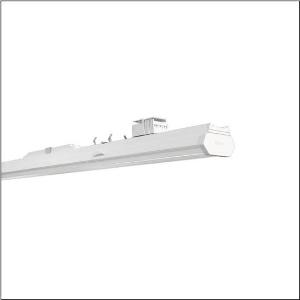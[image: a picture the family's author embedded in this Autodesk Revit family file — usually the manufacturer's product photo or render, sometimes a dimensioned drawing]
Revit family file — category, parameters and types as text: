
# Revit family: licross_11_protected_tw_51tp12tnt85x
name_source: partatom
category: Lighting Fixtures
units: mm (PartAtom-declared; Revit-internal decimal feet)

## family parameters
Cut with Voids When Loaded = No
Host = Face
Light Source = No
Part Type = Normal
Room Calculation Point = No
Round Connector Dimension = Use Diameter
Shared = No

## types (1)
- --- (1 x LED 2700 K ... 6500 K, 8840 lm, 56 W, 2700K)
    Apparent Load = 56 VA
    CIE Flux Codes = 70 91 97 98 100
    Color Rendering = 80
    Color Temperature = 2700K
    Default Elevation = 1800 mm
    Description = Licross 11 Protected TW, luminaire insert, of sheet steel, galvanised, coil coated, white, length: 1.500mm, width: 90mm, height: 101mm, LED rated luminous flux: 8.840lm, light colour: 8tw, SDCM (Standard Deviation of Colour Matching)MacAdam ≤ 2 SDCM (initial), control gear: DALI DT8, with plug, 5-pole, with phase selection, mains connection: 220..240V, AC, 50/60Hz, rated input power: 56W, internal wiring halogen-free, primary optical cover: cover, of PMMA, light emission: direct distribution, primary light characteristic: symmetric, protection rating (complete): IP64, insulation class (complete): insulation class I (protective earthing), certification: CE, ENEC, VDE, UKCA, protection symbol: D if used in an environment with conductive dust loads with corresponding accessories, impact resistance: IK06, permissible ambient temperature for indoor applications: -25..+35°C, corresponds to IFS (International Featured Standards) requirements for safety and quality in the food industry, reducing of maximum allowable ambient temperature of 5°C with ceiling mounting, LABS conformity tested according to VDMA 24364:2018-05, The light source and the operating device comply with the requirements of the Ecodesign Regulation (EU) 2019/2020 and are replaceable in accordance with this regulation, packaging unit: 1 piece
    Height = 92 mm
    Lamp = 1 x LED 2700 K ... 6500 K
    Lamp Light Flux = 8840 lm
    Lamp Power = 56 W
    Lamp count = 1
    Length = 1500 mm
    Luminous efficacy = 158 lm/W
    Manufacturer = Siteco
    ModVariant = No
    Model = 51TP12TNT85X
    Mounting Place = Ceiling
    Mounting Type = Pendant
    Number of Poles = 1
    OnlyDefault = Yes
    Power Factor = 1
    Product Name = Licross 11 Protected TW
    Product group = luminaire insert | ceiling pendant
    ProductGroupID = 901
    Protection Class = Protection class I
    Protection Degree = IP 64
    RLX_Detail_Level = 1
    RLX_Emergency_Light_Flux = 0 lm
    RLX_Emergency_Type = 0
    RLX_Emergency_Type_DB = No
    RlxData = <blob elided: 20993 chars, md5=54ca5dc1>
    Socket = socket
    Standby Power = 0 W
    System Light Flux = 8840 lm
    System Power = 56 W
    Type Comments = individual setting: CCT=2700K
    Type Image = l_1256148.jpg
    URL = http://relux.com
    VarID = @adj_057721
    Voltage = 0 V
    Weight = 0.00 kg
    Width = 88 mm

## geometry (parser evidence)
native form markers: Blend x4, Sweep x11
no freeform markers — native parametric forms only
